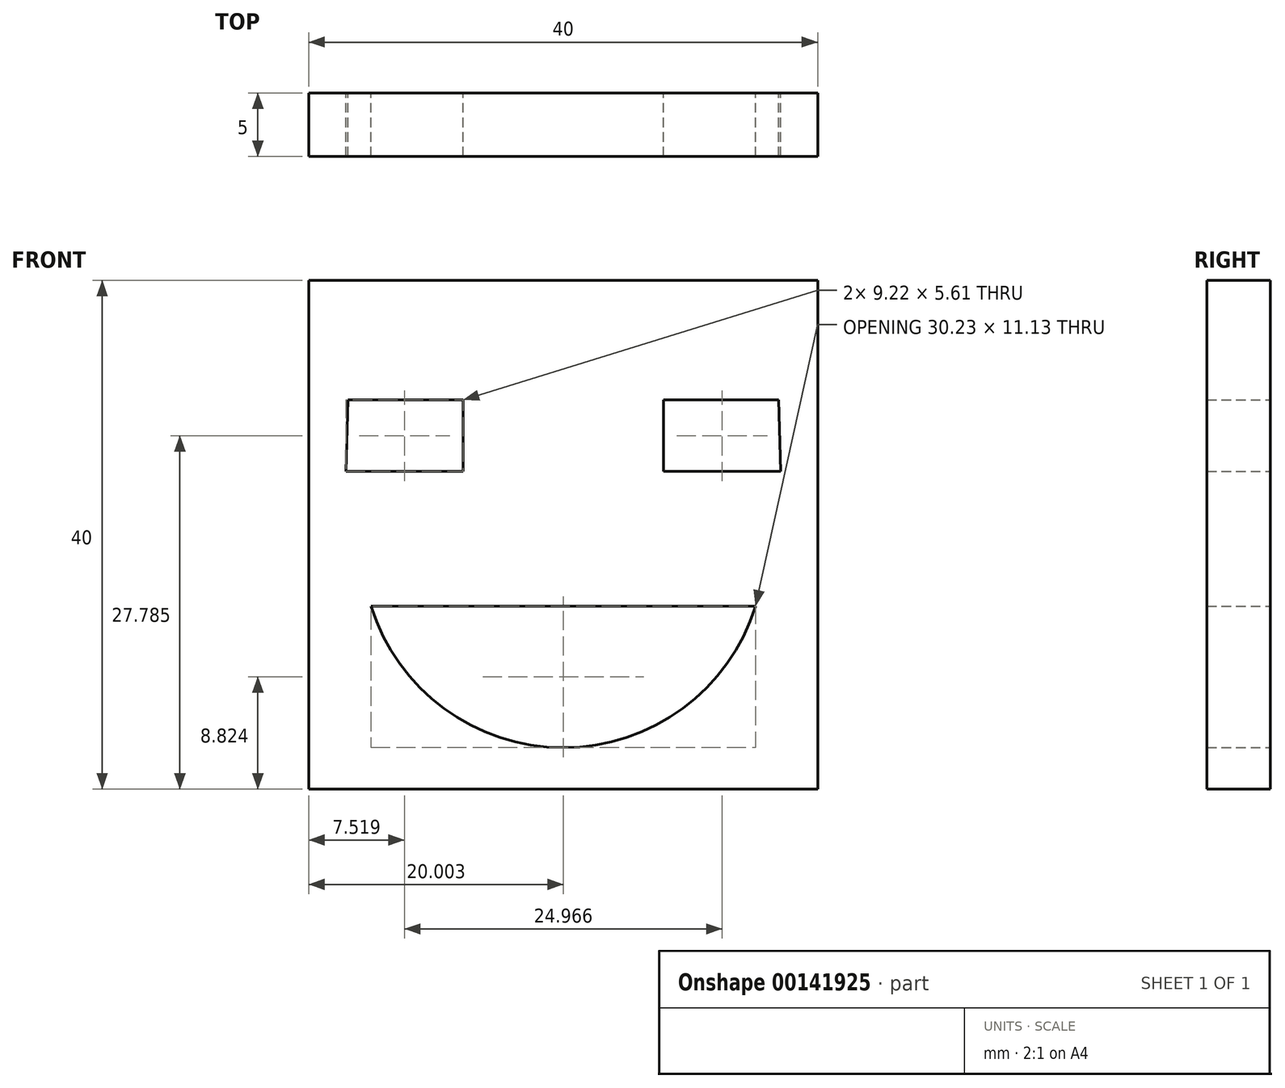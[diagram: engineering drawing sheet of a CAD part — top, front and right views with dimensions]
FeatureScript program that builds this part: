
annotation { "Feature Type Name" : "Feature", "Feature Type Description" : "" }
export const myFeature = defineFeature(function(context is Context, id is Id, definition is map)
    precondition{}
    {
        {
            var Q0;
            Q0=qCreatedBy(makeId("Front.planeOp"),FACE);
            var sketch = newSketch(context, id + "F0", { "sketchPlane" : qUnion([Q0])});
            skLineSegment(sketch, "E0.bottom", {"start": v(-52.39, 50.1) * mm, "end": v(-12.39, 50.1) * mm});
            skLineSegment(sketch, "E0.top", {"start": v(-52.39, 10.1) * mm, "end": v(-12.39, 10.1) * mm});
            skLineSegment(sketch, "E0.left", {"start": v(-52.39, 50.1) * mm, "end": v(-52.39, 10.1) * mm});
            skLineSegment(sketch, "E0.right", {"start": v(-12.39, 50.1) * mm, "end": v(-12.39, 10.1) * mm});
            skLineSegment(sketch, "E1", {"start": v(-49.31, 40.7) * mm, "end": v(-40.26, 40.7) * mm});
            skLineSegment(sketch, "E2", {"start": v(-40.26, 40.7) * mm, "end": v(-40.26, 35.08) * mm});
            skLineSegment(sketch, "E3", {"start": v(-40.26, 35.08) * mm, "end": v(-49.5, 35.08) * mm});
            skLineSegment(sketch, "E4", {"start": v(-49.5, 34.72) * mm, "end": v(-49.31, 40.7) * mm});
            skLineSegment(sketch, "E5.MirrorCS", {"start": v(-15.28, 34.72) * mm, "end": v(-15.46, 40.7) * mm});
            skLineSegment(sketch, "E6.MirrorCS", {"start": v(-15.46, 40.7) * mm, "end": v(-24.51, 40.7) * mm});
            skLineSegment(sketch, "E7.MirrorCS", {"start": v(-24.51, 40.7) * mm, "end": v(-24.51, 35.08) * mm});
            skLineSegment(sketch, "E8.MirrorCS", {"start": v(-24.51, 35.08) * mm, "end": v(-15.28, 35.08) * mm});
            skPoint(sketch, "E9.end.orphan", {"position": v(-44.79, 35.08) * mm});
            skPoint(sketch, "E9.start.orphan", {"position": v(-44.79, 40.7) * mm});
            skPoint(sketch, "E10.MirrorCS.end.orphan", {"position": v(-19.99, 35.08) * mm});
            skPoint(sketch, "E10.MirrorCS.start.orphan", {"position": v(-19.99, 40.7) * mm});
            skArc(sketch, "E11", {"start": v(-47.5, 24.5) * mm, "mid": v(-32.39, 13.36) * mm, "end": v(-17.27, 24.5) * mm});
            skLineSegment(sketch, "E12", {"start": v(-47.5, 24.5) * mm, "end": v(-17.27, 24.5) * mm});
            skSolve(sketch);
        }
        {
            var Q0;
            Q0=qSketchRegion(id+"F0",true);
            extrude(context, id + "F1", {"entities" : qUnion([Q0]), "depth" : 5 * mm});
        }
    });
